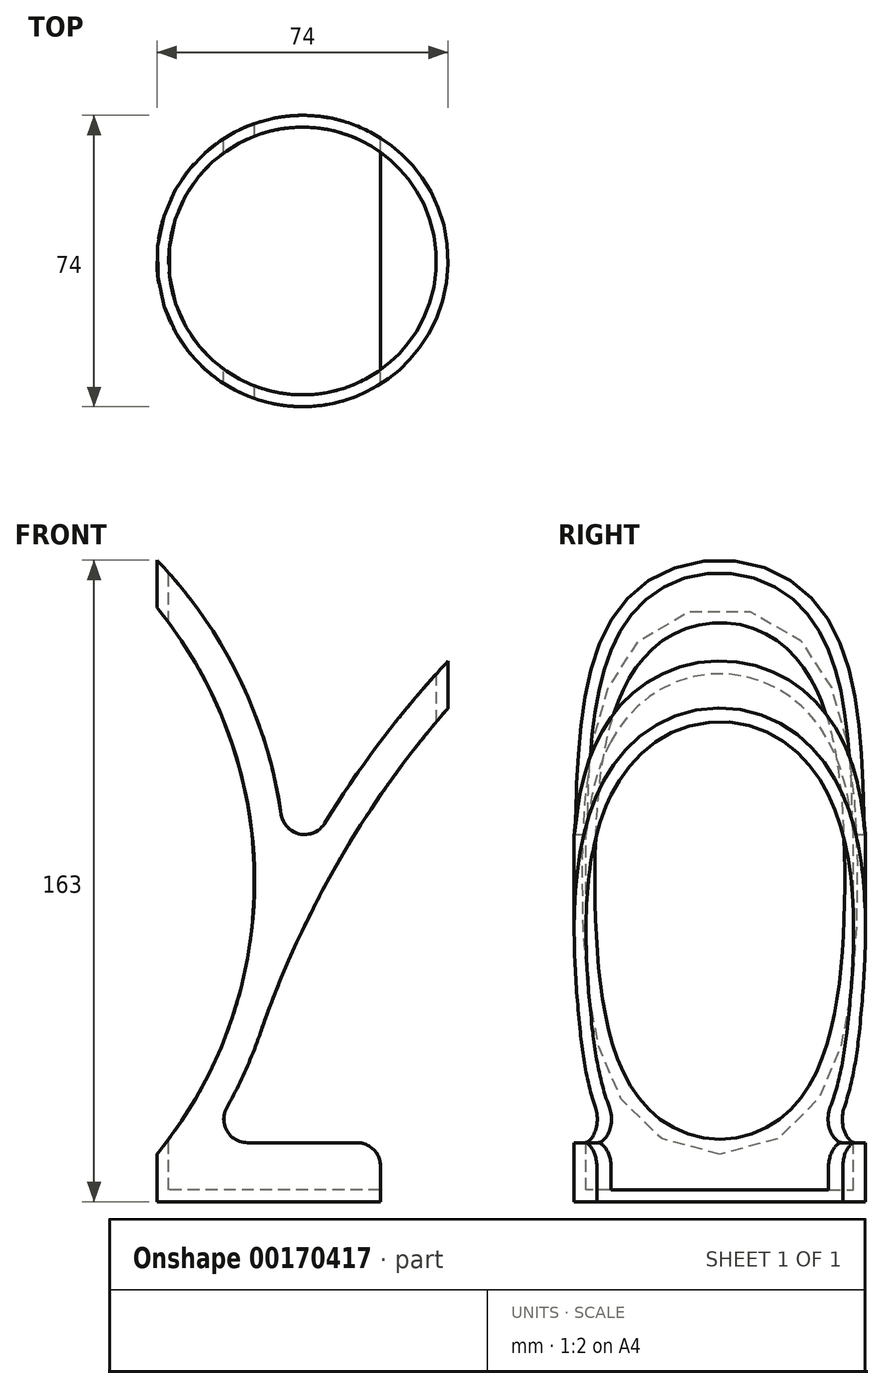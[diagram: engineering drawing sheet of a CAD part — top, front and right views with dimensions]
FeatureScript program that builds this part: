
annotation { "Feature Type Name" : "Feature", "Feature Type Description" : "" }
export const myFeature = defineFeature(function(context is Context, id is Id, definition is map)
    precondition{}
    {
        {
            var Q0;
            Q0=qCreatedBy(makeId("Front.planeOp"),FACE);
            var sketch = newSketch(context, id + "F0", { "sketchPlane" : qUnion([Q0])});
            skLineSegment(sketch, "E0.bottom", {"start": v(0, -81.5) * mm, "end": v(-37, -81.5) * mm});
            skLineSegment(sketch, "E0.right", {"start": v(-37, -81.5) * mm, "end": v(-37, 81.5) * mm});
            skPoint(sketch, "E0.middle", {"position": v(0, 0) * mm});
            skLineSegment(sketch, "E1.0", {"start": v(-34, -78.5) * mm, "end": v(-34, 81.5) * mm});
            skLineSegment(sketch, "E1.1", {"start": v(0, -78.5) * mm, "end": v(-34, -78.5) * mm});
            skLineSegment(sketch, "E2.trimOffspring", {"start": v(-34, 81.5) * mm, "end": v(-37, 81.5) * mm});
            skPoint(sketch, "E3.endSnap0", {"position": v(0, -81.5) * mm});
            skLineSegment(sketch, "E4.trimOffspring", {"start": v(0, -78.5) * mm, "end": v(0, -81.5) * mm});
            skSolve(sketch);
        }
        {
            var Q0;
            Q0 = qSketchRegion(id + "F0", true);
            var Q1;
            Q1=sQuery(id+"F0.wireOp",EDGE,"E4.trimOffspring");
            revolve(context, id + "F1", {"entities" : qUnion([Q0]), "axis" : qUnion([Q1]), "revolveType" : RevolveType.FULL});
        }
        {
            var Q0;
            Q0=qCreatedBy(makeId("Front.planeOp"),FACE);
            var sketch = newSketch(context, id + "F2", { "sketchPlane" : qUnion([Q0])});
            skArc(sketch, "E5", {"start": v(-19.24, -57.56) * mm, "mid": v(-14.52, -48.2) * mm, "end": v(-10.66, -38.45) * mm});
            skArc(sketch, "E6.0", {"start": v(-37, -69.45) * mm, "mid": v(-12.2, 0) * mm, "end": v(-37, 69.45) * mm});
            skArc(sketch, "E7", {"start": v(37, 55.9) * mm, "mid": v(20.28, 36.06) * mm, "end": v(5.63, 14.65) * mm});
            skArc(sketch, "E8.0", {"start": v(37, 43.95) * mm, "mid": v(9.21, 5.03) * mm, "end": v(-10.66, -38.45) * mm});
            skLineSegment(sketch, "E9", {"start": v(37, 81.5) * mm, "end": v(37, -81.5) * mm, "construction": true});
            skLineSegment(sketch, "E10", {"start": v(37, 55.9) * mm, "end": v(37, 43.95) * mm});
            skArc(sketch, "E11", {"start": v(-5.42, 16.92) * mm, "mid": v(-16.16, 51.68) * mm, "end": v(-37, 81.5) * mm});
            skPoint(sketch, "E12.visualSharp", {"position": v(-4.24, -2.96) * mm});
            skArc(sketch, "E12.filletArc", {"start": v(-5.42, 16.92) * mm, "mid": v(-0.7, 11.91) * mm, "end": v(5.63, 14.65) * mm});
            skLineSegment(sketch, "E13", {"start": v(-37, -81.5) * mm, "end": v(19.8, -81.5) * mm});
            skLineSegment(sketch, "E14", {"start": v(19.8, -81.5) * mm, "end": v(19.8, -72.5) * mm});
            skLineSegment(sketch, "E15", {"start": v(13.8, -66.5) * mm, "end": v(-14.01, -66.5) * mm});
            skPoint(sketch, "E16.visualSharp", {"position": v(-24.8, -66.5) * mm});
            skArc(sketch, "E16.filletArc", {"start": v(-19.24, -57.56) * mm, "mid": v(-19.19, -63.53) * mm, "end": v(-14.01, -66.5) * mm});
            skPoint(sketch, "E17.visualSharp", {"position": v(19.8, -66.5) * mm});
            skArc(sketch, "E17.filletArc", {"start": v(19.8, -72.5) * mm, "mid": v(18.04, -68.26) * mm, "end": v(13.8, -66.5) * mm});
            skLineSegment(sketch, "E18", {"start": v(-37, 81.5) * mm, "end": v(-37, 69.45) * mm});
            skLineSegment(sketch, "E19", {"start": v(-37, -69.45) * mm, "end": v(-37, -81.5) * mm});
            skSolve(sketch);
        }
        {
            var Q0;
            Q0 = qSketchRegion(id + "F2", true);
            extrude(context, id + "F3", {"entities" : qUnion([Q0]), "operationType" : NewBodyOperationType.INTERSECT, "endBound" : BoundingType.SYMMETRIC, "depth" : 80 * mm});
        }
    });
